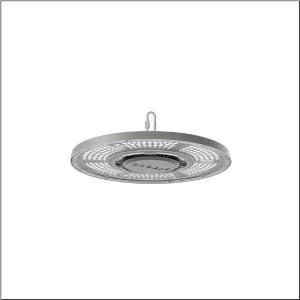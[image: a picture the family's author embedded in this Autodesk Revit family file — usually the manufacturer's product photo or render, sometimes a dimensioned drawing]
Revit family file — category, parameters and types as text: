
# Revit family: highbay_31-s_51hc417a4fmb
name_source: partatom
category: Lighting Fixtures
units: mm (PartAtom-declared; Revit-internal decimal feet)

## family parameters
Cut with Voids When Loaded = No
Host = Face
Light Source = No
Part Type = Normal
Room Calculation Point = No
Round Connector Dimension = Use Diameter
Shared = No

## types (1)
- Highbay 31-S (1 x LED, 14000 lm, 94 W, 4000K)
    Apparent Load = 94 VA
    CIE Flux Codes = 94 98 100 100 100
    Color Rendering = 80
    Color Temperature = 4000K
    Default Elevation = 1800 mm
    Description = Highbay 31-S, LED high bay luminaire, primary light control with lens, of PC, primary optical cover: cover panel, of PC, transparent, light emission: direct distribution, primary light characteristic: rotationally symmetric, installation type: suspended mounting, surface-mounted, LED, rated luminous flux: 14.000lm, luminous efficacy: 150lm/W, light colour: 840, colour temperature: 4000K, control gear: ECG, with cable, 3x 1.0mm², free wire ends, mains connection: 220..240V, AC/DC, 0/50..60Hz, cable length: 1,5m, rated input power: 94W, housing, rotationally symmetric, of diecast aluminium, powder-coated, grey aluminium (RAL 9007), with hook on luminaire side, incl. screw, diameter: 339mm, protection rating (complete): IP65, insulation class (complete): insulation class I (protective earthing), certification: CE, ENEC, UKCA, protection symbol: D, impact resistance: IK08, permissible operating ambient temperature: -30..+45°C, standard: EN 60598-2-22, EN 60598, corresponds to IFS (International Featured Standards) requirements for safety and quality in the food industry, packaging unit: 1 piece
    Height = 141 mm
    Lamp = 1 x LED
    Lamp Light Flux = 14000 lm
    Lamp Power = 94 W
    Lamp count = 1
    Length = 339 mm
    Luminous efficacy = 149 lm/W
    Manufacturer = Siteco
    ModVariant = No
    Model = 51HC417A4FMB
    Mounting Place = Ceiling
    Mounting Type = Pendant
    Number of Poles = 1
    OnlyDefault = Yes
    Power Factor = 1
    Product Name = Highbay 31-S
    Product group = LED high bay luminaire
    ProductGroupID = 903
    Protection Class = Protection class I
    Protection Degree = IP 65
    RLX_Detail_Level = 1
    RLX_Emergency_Light_Flux = 0 lm
    RLX_Emergency_Type = 0
    RLX_Emergency_Type_DB = No
    RlxData = <blob elided: 106537 chars, md5=a07ec3ea>
    Socket = socket
    Standby Power = 0 W
    System Light Flux = 14000 lm
    System Power = 94 W
    Type Comments = Product without accessories
    Type Image = l_1007237.jpg
    URL = http://relux.com
    VarID = ---
    Voltage = 0 V
    Weight = 0.00 kg
    Width = 0 mm  [stored 0 ft]

note: [stored X ft] marks values corroborated as IEEE doubles in the binary element streams (Revit-internal decimal feet)

## geometry (parser evidence)
native form markers: Blend x4, Sweep x9
no freeform markers — native parametric forms only
